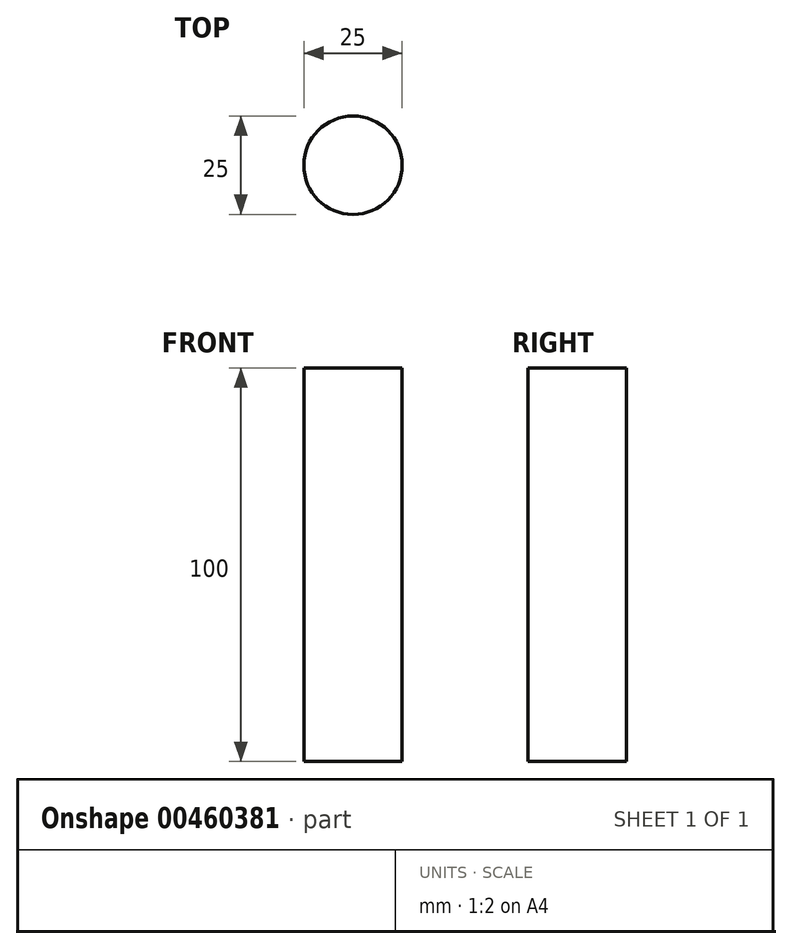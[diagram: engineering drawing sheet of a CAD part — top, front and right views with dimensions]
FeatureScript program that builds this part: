
annotation { "Feature Type Name" : "Feature", "Feature Type Description" : "" }
export const myFeature = defineFeature(function(context is Context, id is Id, definition is map)
    precondition{}
    {
        {
            var Q0;
            Q0=qCreatedBy(makeId("Top.planeOp"),FACE);
            var sketch = newSketch(context, id + "F0", { "sketchPlane" : qUnion([Q0])});
            skCircle(sketch, "E0", {"center": v(0, 0) * mm, "radius": 12.5 * mm});
            skSolve(sketch);
        }
        {
            var Q0;
            Q0 = qSketchRegion(id + "F0", true);
            extrude(context, id + "F1", {"entities" : qUnion([Q0]), "depth" : 100 * mm});
        }
    });
